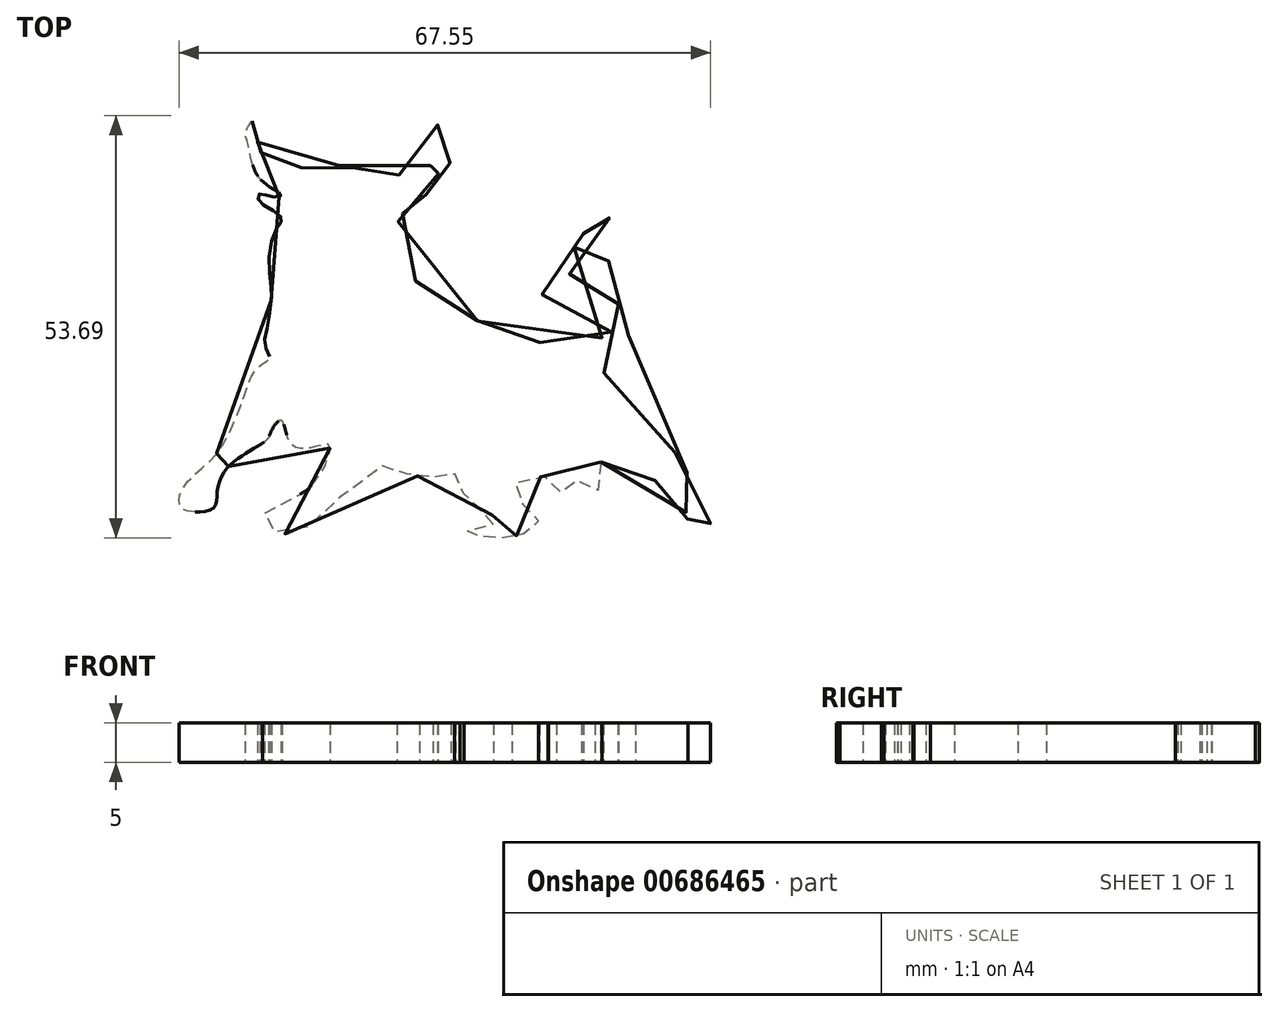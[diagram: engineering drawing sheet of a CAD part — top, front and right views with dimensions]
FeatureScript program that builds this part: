
annotation { "Feature Type Name" : "Feature", "Feature Type Description" : "" }
export const myFeature = defineFeature(function(context is Context, id is Id, definition is map)
    precondition{}
    {
        {
            var Q0;
            Q0=qCreatedBy(makeId("Top.planeOp"),FACE);
            var sketch = newSketch(context, id + "F0", { "sketchPlane" : qUnion([Q0])});
            skPoint(sketch, "E0.90.internal.snap0", {"position": v(-68.44, 27.16) * mm});
            skPoint(sketch, "E0.142.internal.snap0", {"position": v(-34.22, 54.32) * mm});
            skPoint(sketch, "E0.147.internal.snap0", {"position": v(-34.22, 54.32) * mm});
            skPoint(sketch, "E0.171.internal.snap0", {"position": v(-68.44, 27.16) * mm});
            skPoint(sketch, "E0.172.internal.snap0", {"position": v(-68.44, 27.16) * mm});
            skPoint(sketch, "E0.180.internal.snap0", {"position": v(-68.44, 27.16) * mm});
            skFitSpline(sketch, "E0", {"points": [v(-14.3, 10.15) * mm, v(-14.15, 8.73) * mm, v(-14.5, 6.73) * mm, v(-15.03, 6.53) * mm, v(-16.2, 7.02) * mm, v(-17.23, 7.85) * mm, v(-17.72, 7.36) * mm, v(-18.06, 6.83) * mm, v(-18.75, 6.24) * mm, v(-20.21, 6.83) * mm, v(-21, 7.85) * mm, v(-21, 8.15) * mm, v(-22.16, 8.3) * mm, v(-23.58, 8.1) * mm, v(-25.34, 7.32) * mm, v(-25.44, 6.2) * mm, v(-24.7, 5.36) * mm, v(-23.83, 4.39) * mm, v(-23.14, 3.7) * mm, v(-22.31, 2.97) * mm, v(-22.26, 2.24) * mm, v(-22.9, 1.8) * mm, v(-23.68, 1.21) * mm, v(-24.5, 0.92) * mm, v(-25.93, 0.62) * mm, v(-26.27, 0.62) * mm, v(-27, 0.53) * mm, v(-27.73, 0.53) * mm, v(-28.42, 0.53) * mm, v(-29.59, 0.72) * mm, v(-30.86, 0.72) * mm, v(-31.64, 0.97) * mm, v(-31.6, 1.16) * mm, v(-30.52, 1.6) * mm, v(-29.64, 1.7) * mm, v(-28.03, 2.28) * mm, v(-28.03, 2.97) * mm, v(-28.32, 3.9) * mm, v(-30.08, 4.58) * mm, v(-30.45, 5.09) * mm, v(-31.1, 5.3) * mm, v(-31.66, 6.02) * mm, v(-32.15, 6.73) * mm, v(-32.15, 6.73) * mm, v(-32.86, 8.05) * mm, v(-32.76, 8.59) * mm, v(-33.3, 8.63) * mm, v(-34.03, 8.44) * mm, v(-35.1, 8.24) * mm, v(-36.67, 8.34) * mm, v(-37.9, 8.44) * mm, v(-38.92, 8.63) * mm, v(-40.04, 9.07) * mm, v(-41.65, 9.76) * mm, v(-42.44, 9.32) * mm, v(-47.52, 5.6) * mm, v(-50.39, 3.47) * mm, v(-52.48, 1) * mm, v(-54.95, 1.17) * mm, v(-56.57, 1.58) * mm, v(-57.25, 2.6) * mm, v(-56.96, 3.7) * mm, v(-54.17, 4.96) * mm, v(-52.17, 6.28) * mm, v(-51.56, 6.69) * mm, v(-49.34, 9.63) * mm, v(-49.16, 10.28) * mm, v(-48.7, 11.79) * mm, v(-48.98, 12.4) * mm, v(-50.78, 12.06) * mm, v(-53.68, 12.48) * mm, v(-54.85, 15.45) * mm, v(-55.96, 14.48) * mm, v(-56.65, 13.1) * mm, v(-58.1, 12.06) * mm, v(-59.97, 10.89) * mm, v(-61.9, 9.23) * mm, v(-63, 6.54) * mm, v(-63.35, 4.46) * mm, v(-65.63, 3.84) * mm, v(-67.5, 4.26) * mm, v(-67.84, 5.02) * mm, v(-67.84, 5.85) * mm, v(-66.32, 8.2) * mm, v(-63.42, 10.82) * mm, v(-60.86, 15.3) * mm, v(-59.24, 19.6) * mm, v(-57.76, 22.32) * mm, v(-56.36, 23.39) * mm, v(-56.94, 24.86) * mm, v(-56.7, 27.16) * mm, v(-56.2, 30.29) * mm, v(-56.12, 31.85) * mm, v(-56.44, 36.45) * mm, v(-55.21, 40.3) * mm, v(-54.8, 40.97) * mm, v(-55.87, 42.12) * mm, v(-57.76, 43.35) * mm, v(-57.76, 44.17) * mm, v(-57.02, 44.17) * mm, v(-55.62, 43.84) * mm, v(-54.88, 44.09) * mm, v(-55.7, 44.74) * mm, v(-58, 46.72) * mm, v(-59.24, 50.99) * mm, v(-59.4, 52.14) * mm, v(-57.99, 54.13) * mm, v(-57.71, 54.16) * mm, v(-57.6, 53.81) * mm, v(-57.84, 52.68) * mm, v(-57.89, 51.17) * mm, v(-57.9, 50.87) * mm, v(-57.87, 50.2) * mm, v(-57.67, 49.72) * mm, v(-57.06, 49.1) * mm, v(-56.4, 48.53) * mm, v(-55.93, 48.1) * mm, v(-55.7, 47.95) * mm, v(-54.88, 47.53) * mm, v(-53.72, 46.93) * mm, v(-52.95, 47.3) * mm, v(-51.92, 47.69) * mm, v(-49.54, 48) * mm, v(-48.5, 48.12) * mm, v(-47.27, 47.73) * mm, v(-46.92, 47.66) * mm, v(-46.23, 47.53) * mm, v(-45.56, 47.53) * mm, v(-44.93, 47.6) * mm, v(-44.59, 47.9) * mm, v(-44.3, 48) * mm, v(-43.4, 48.2) * mm, v(-43.07, 48.14) * mm, v(-42.45, 48.06) * mm, v(-40.83, 47.04) * mm, v(-39.85, 46.62) * mm, v(-37.38, 47.2) * mm, v(-35.82, 47.94) * mm, v(-35.33, 49.66) * mm, v(-35, 51.64) * mm, v(-34.92, 53.67) * mm, v(-34.53, 53.34) * mm, v(-34.22, 52.74) * mm, v(-33.93, 51.8) * mm, v(-33.65, 50.55) * mm, v(-33.42, 49.62) * mm, v(-33.4, 48.23) * mm, v(-34.22, 47.16) * mm, v(-35.12, 46.73) * mm, v(-36.34, 46.32) * mm, v(-37.1, 45.7) * mm, v(-37.3, 44.88) * mm, v(-37.01, 44.39) * mm, v(-36.2, 44) * mm, v(-35.62, 43.34) * mm, v(-35.78, 42.85) * mm, v(-36.17, 42.72) * mm, v(-36.66, 42.58) * mm, v(-36.97, 42.46) * mm, v(-38.43, 42.27) * mm, v(-38.86, 42.19) * mm, v(-39.77, 41.39) * mm, v(-40.13, 40.01) * mm, v(-40.18, 38.9) * mm, v(-39.58, 36.35) * mm, v(-38.43, 33.55) * mm, v(-36.54, 32.73) * mm, v(-34.9, 32) * mm, v(-33.26, 30.84) * mm, v(-31.37, 29.37) * mm, v(-29.89, 28.05) * mm, v(-28.74, 27.16) * mm, v(-27.84, 27.16) * mm, v(-25.45, 26.24) * mm, v(-23.73, 25.67) * mm, v(-22, 25.34) * mm, v(-20.03, 24.68) * mm, v(-19.79, 24.6) * mm, v(-17.4, 23.53) * mm, v(-14.28, 25.83) * mm, v(-12.4, 27.16) * mm, v(-12.15, 28.22) * mm, v(-13.95, 29.04) * mm, v(-20.28, 30.43) * mm, v(-22.09, 32.32) * mm, v(-21.1, 34.62) * mm, v(-18.72, 36.6) * mm, v(-16.66, 38.48) * mm, v(-16.5, 39.14) * mm, v(-16.66, 42.1) * mm, v(-15.1, 43.25) * mm, v(-13.95, 43.5) * mm, v(-14.12, 42.92) * mm, v(-13.54, 41.69) * mm, v(-12.47, 39.55) * mm, v(-12.3, 36.27) * mm, v(-14.53, 35.53) * mm, v(-18.14, 34.13) * mm, v(-19.87, 32.98) * mm, v(-19.3, 32) * mm, v(-15.51, 31.17) * mm, v(-13.13, 30.52) * mm, v(-10.1, 29.04) * mm, v(-11.49, 25.5) * mm, v(-15.02, 22.55) * mm, v(-13.3, 21.07) * mm, v(-9.27, 15.98) * mm, v(-6.67, 12.17) * mm, v(-5.04, 11.47) * mm, v(-3.65, 9.73) * mm, v(-2.72, 6.24) * mm, v(-1.56, 3.69) * mm, v(-0.52, 2.73) * mm, v(-0.35, 1.76) * mm, v(-0.45, 1) * mm, v(-1.18, 0.9) * mm, v(-1.8, 0.86) * mm, v(-2.73, 0.86) * mm, v(-3.22, 1.59) * mm, v(-3.15, 2.45) * mm, v(-3.36, 3.21) * mm, v(-3.56, 3.97) * mm, v(-4.29, 4.46) * mm, v(-5.12, 5.32) * mm, v(-5.5, 6.08) * mm, v(-6.3, 7.46) * mm, v(-7.3, 7.77) * mm, v(-8.78, 8.46) * mm, v(-10.75, 9.43) * mm, v(-11.23, 9.95) * mm, v(-12.23, 10.3) * mm, v(-13.75, 10.22) * mm, v(-14.3, 10.15) * mm]});
            skSolve(sketch);
        }
        {
            var Q0;
            Q0 = qSketchRegion(id + "F0", true);
            extrude(context, id + "F1", {"entities" : qUnion([Q0]), "depth" : 5 * mm, "offsetDistance" : 25.4 * mm});
        }
    });
